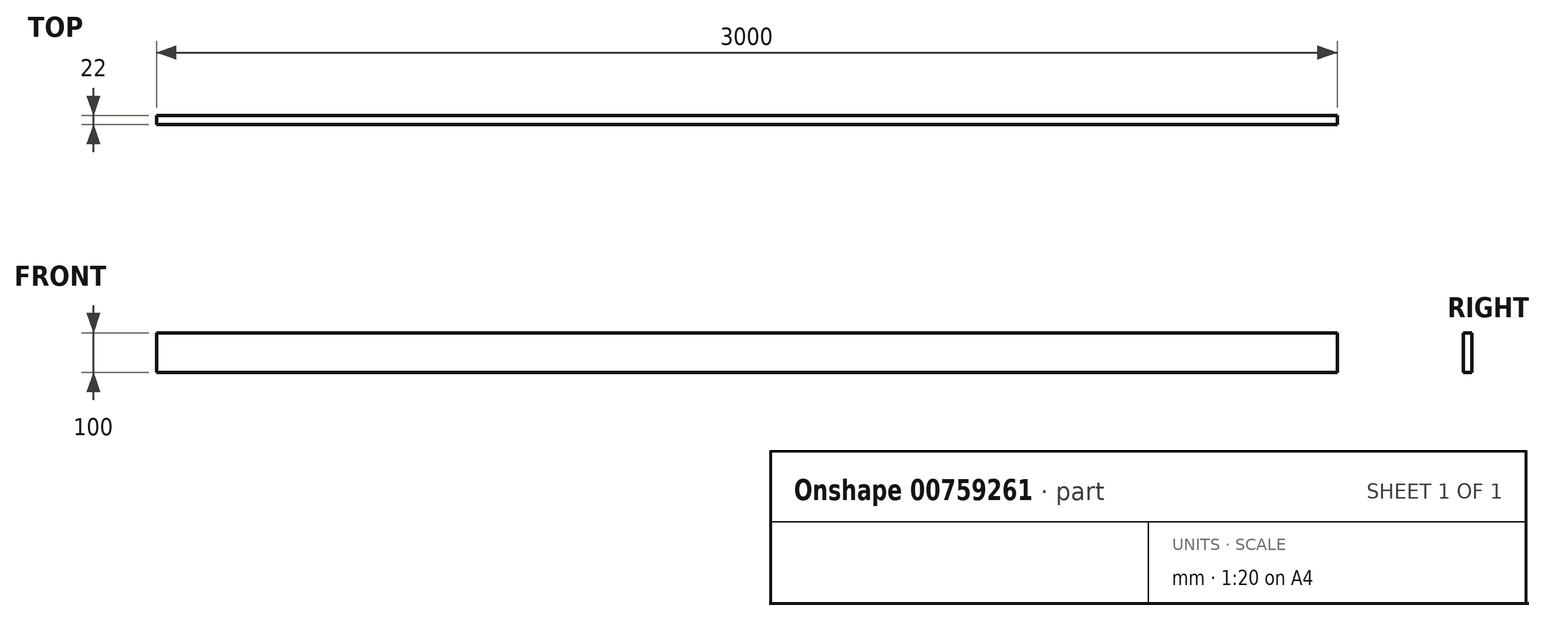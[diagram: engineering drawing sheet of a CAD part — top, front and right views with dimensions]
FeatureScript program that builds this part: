
annotation { "Feature Type Name" : "Feature", "Feature Type Description" : "" }
export const myFeature = defineFeature(function(context is Context, id is Id, definition is map)
    precondition{}
    {
        {
            var Q0;
            Q0=qCreatedBy(makeId("Front.planeOp"),FACE);
            var sketch = newSketch(context, id + "F0", { "sketchPlane" : qUnion([Q0])});
            skLineSegment(sketch, "E0.bottom", {"start": v(0, 0) * mm, "end": v(3000, 0) * mm});
            skLineSegment(sketch, "E0.top", {"start": v(0, 100) * mm, "end": v(3000, 100) * mm});
            skLineSegment(sketch, "E0.left", {"start": v(0, 0) * mm, "end": v(0, 100) * mm});
            skLineSegment(sketch, "E0.right", {"start": v(3000, 0) * mm, "end": v(3000, 100) * mm});
            skSolve(sketch);
        }
        {
            var Q0;
            Q0 = qSketchRegion(id + "F0", true);
            extrude(context, id + "F1", {"entities" : qUnion([Q0]), "depth" : 22 * mm, "offsetDistance" : 25 * mm});
        }
    });
